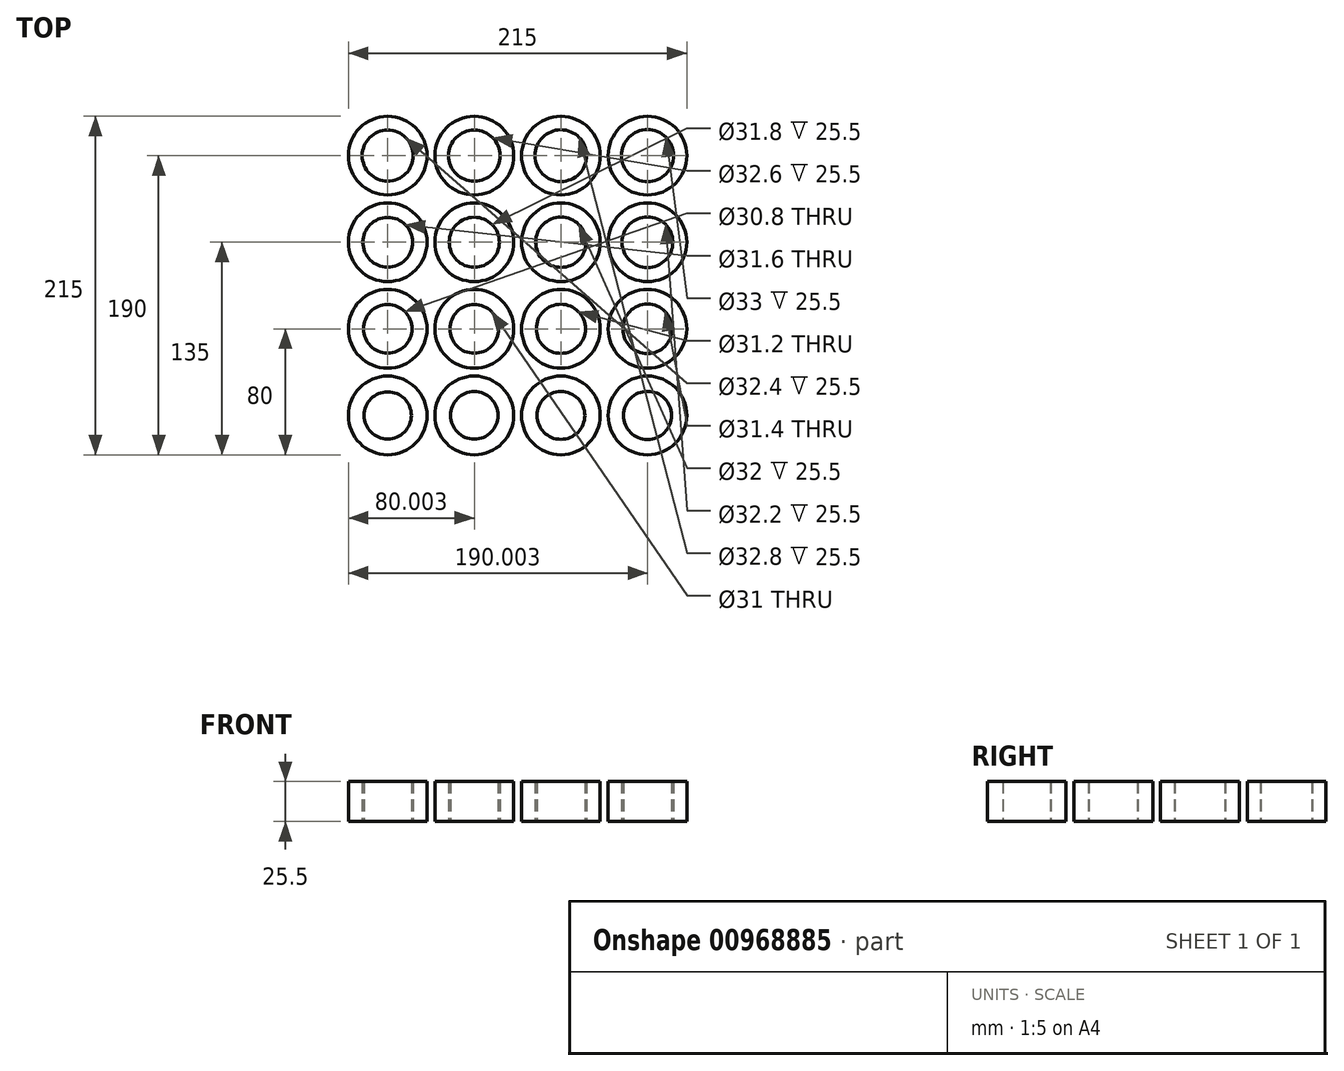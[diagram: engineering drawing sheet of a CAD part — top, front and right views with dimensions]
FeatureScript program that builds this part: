
annotation { "Feature Type Name" : "Feature", "Feature Type Description" : "" }
export const myFeature = defineFeature(function(context is Context, id is Id, definition is map)
    precondition{}
    {
        {
            var Q0;
            Q0=qCreatedBy(makeId("Top.planeOp"),FACE);
            var sketch = newSketch(context, id + "F0", { "sketchPlane" : qUnion([Q0])});
            skCircle(sketch, "E0", {"center": v(-156.6, 0) * mm, "radius": 25 * mm});
            skCircle(sketch, "E1", {"center": v(-156.6, 0) * mm, "radius": 15 * mm});
            skCircle(sketch, "E2.0.1.0", {"center": v(-156.6, 55) * mm, "radius": 25 * mm});
            skCircle(sketch, "E2.0.2.0", {"center": v(-156.6, 110) * mm, "radius": 25 * mm});
            skCircle(sketch, "E2.0.3.0", {"center": v(-156.6, 165) * mm, "radius": 25 * mm});
            skCircle(sketch, "E2.1.0.0", {"center": v(-101.6, 0) * mm, "radius": 25 * mm});
            skCircle(sketch, "E2.1.1.0", {"center": v(-101.6, 55) * mm, "radius": 25 * mm});
            skCircle(sketch, "E2.1.2.0", {"center": v(-101.6, 110) * mm, "radius": 25 * mm});
            skCircle(sketch, "E2.1.3.0", {"center": v(-101.6, 165) * mm, "radius": 25 * mm});
            skCircle(sketch, "E2.2.0.0", {"center": v(-46.6, 0) * mm, "radius": 25 * mm});
            skCircle(sketch, "E2.2.1.0", {"center": v(-46.6, 55) * mm, "radius": 25 * mm});
            skCircle(sketch, "E2.2.2.0", {"center": v(-46.6, 110) * mm, "radius": 25 * mm});
            skCircle(sketch, "E2.2.3.0", {"center": v(-46.6, 165) * mm, "radius": 25 * mm});
            skCircle(sketch, "E2.3.0.0", {"center": v(8.4, 0) * mm, "radius": 25 * mm});
            skCircle(sketch, "E2.3.1.0", {"center": v(8.4, 55) * mm, "radius": 25 * mm});
            skCircle(sketch, "E2.3.2.0", {"center": v(8.4, 110) * mm, "radius": 25 * mm});
            skCircle(sketch, "E2.3.3.0", {"center": v(8.4, 165) * mm, "radius": 25 * mm});
            skLineSegment(sketch, "E2.direction2", {"start": v(-156.6, 0) * mm, "end": v(-156.6, 55) * mm, "construction": true});
            skCircle(sketch, "E3", {"center": v(-101.6, 0) * mm, "radius": 15.1 * mm});
            skCircle(sketch, "E4", {"center": v(-46.6, 0) * mm, "radius": 15.2 * mm});
            skCircle(sketch, "E5", {"center": v(8.4, 0) * mm, "radius": 15.3 * mm});
            skCircle(sketch, "E6", {"center": v(-156.6, 55) * mm, "radius": 15.4 * mm});
            skCircle(sketch, "E7", {"center": v(-101.6, 55) * mm, "radius": 15.5 * mm});
            skCircle(sketch, "E8", {"center": v(-46.6, 55) * mm, "radius": 15.6 * mm});
            skCircle(sketch, "E9", {"center": v(8.4, 55) * mm, "radius": 15.7 * mm});
            skCircle(sketch, "E10", {"center": v(-156.6, 110) * mm, "radius": 15.8 * mm});
            skCircle(sketch, "E11", {"center": v(-101.6, 110) * mm, "radius": 15.9 * mm});
            skCircle(sketch, "E12", {"center": v(-46.6, 110) * mm, "radius": 16 * mm});
            skCircle(sketch, "E13", {"center": v(8.4, 110) * mm, "radius": 16.1 * mm});
            skCircle(sketch, "E14", {"center": v(-156.6, 165) * mm, "radius": 16.2 * mm});
            skCircle(sketch, "E15", {"center": v(-101.6, 165) * mm, "radius": 16.3 * mm});
            skCircle(sketch, "E16", {"center": v(-46.6, 165) * mm, "radius": 16.4 * mm});
            skCircle(sketch, "E17", {"center": v(8.4, 165) * mm, "radius": 16.5 * mm});
            skLineSegment(sketch, "E18.trimOffspring", {"start": v(-116.7, 0) * mm, "end": v(-101.6, 0) * mm});
            skSolve(sketch);
        }
        {
            var Q0;
            Q0 = qSketchRegion(id + "F0", true);
            extrude(context, id + "F1", {"entities" : qUnion([Q0]), "depth" : 25.5 * mm, "offsetDistance" : 25 * mm});
        }
    });
